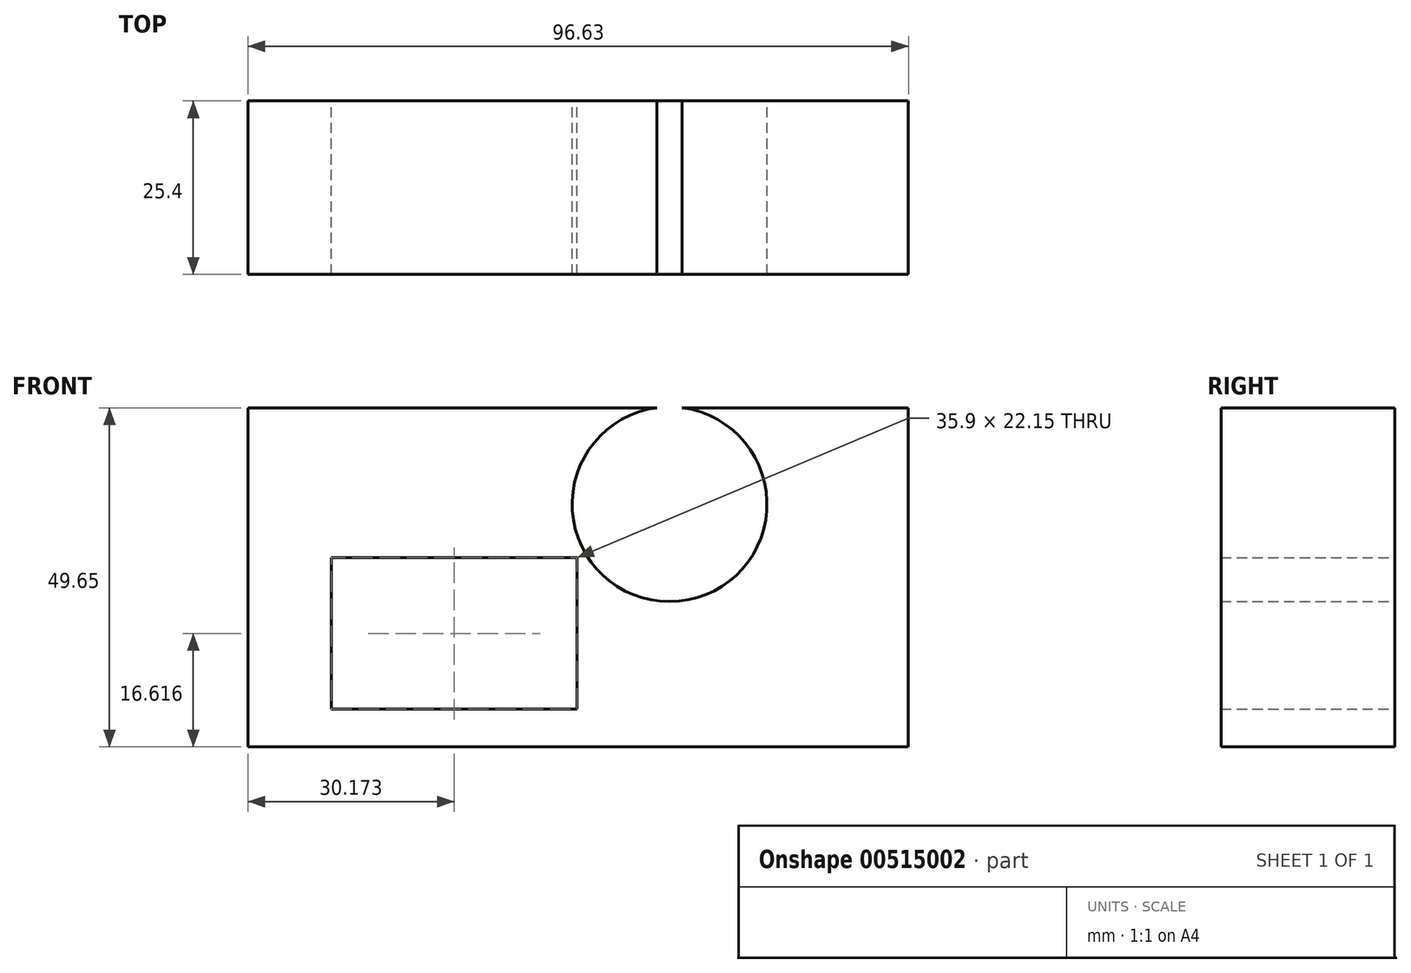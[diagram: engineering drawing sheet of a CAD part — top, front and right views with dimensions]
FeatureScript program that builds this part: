
annotation { "Feature Type Name" : "Feature", "Feature Type Description" : "" }
export const myFeature = defineFeature(function(context is Context, id is Id, definition is map)
    precondition{}
    {
        {
            var Q0;
            Q0=qCreatedBy(makeId("Front.planeOp"),FACE);
            var sketch = newSketch(context, id + "F0", { "sketchPlane" : qUnion([Q0])});
            skLineSegment(sketch, "E0.bottom", {"start": v(-43.54, 14.13) * mm, "end": v(53.09, 14.13) * mm});
            skLineSegment(sketch, "E0.top", {"start": v(-43.54, -35.52) * mm, "end": v(53.09, -35.52) * mm});
            skLineSegment(sketch, "E0.left", {"start": v(-43.54, 14.13) * mm, "end": v(-43.54, -35.52) * mm});
            skLineSegment(sketch, "E0.right", {"start": v(53.09, 14.13) * mm, "end": v(53.09, -35.52) * mm});
            skCircle(sketch, "E1", {"center": v(18.14, 0) * mm, "radius": 14.25 * mm});
            skLineSegment(sketch, "E2.bottom", {"start": v(-31.32, -7.83) * mm, "end": v(4.58, -7.83) * mm});
            skLineSegment(sketch, "E2.top", {"start": v(-31.32, -29.98) * mm, "end": v(4.58, -29.98) * mm});
            skLineSegment(sketch, "E2.left", {"start": v(-31.32, -7.83) * mm, "end": v(-31.32, -29.98) * mm});
            skLineSegment(sketch, "E2.right", {"start": v(4.58, -7.83) * mm, "end": v(4.58, -29.98) * mm});
            skSolve(sketch);
        }
        {
            var Q0;
            Q0=makeQuery(id+"F0.imprint","IMPRINT",FACE,{"disambiguationData":[TD([[makeQuery(id+"F0.imprint","IMPRINT",EDGE,{"derivedFrom":sQuery(id+"F0.wireOp",EDGE,"E0.top")}),1.0]])]});
            extrude(context, id + "F1", {"entities" : qUnion([Q0]), "depth" : 25.4 * mm, "offsetDistance" : 25.4 * mm});
        }
    });
